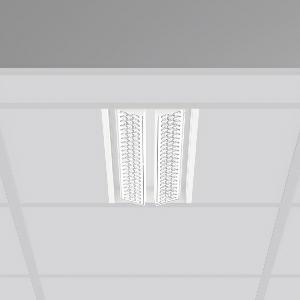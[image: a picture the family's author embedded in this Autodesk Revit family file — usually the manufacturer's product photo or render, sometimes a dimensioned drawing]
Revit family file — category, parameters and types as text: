
# Revit family: tx-move_901736_002_25e7
name_source: partatom
category: Lighting Fixtures
units: mm (PartAtom-declared; Revit-internal decimal feet)

## family parameters
Cut with Voids When Loaded = No
Host = Face
Light Source = No
Part Type = Normal
Room Calculation Point = No
Round Connector Dimension = Use Diameter
Shared = No

## types (1)
- MultiLumen 1 (1 x LED Modul 830, 2750 lm, 3000)
    Apparent Load = 35 VA
    Approval mark = CE
    CIE Flux Codes = 90 97 99 100 100
    Color Rendering = 80
    Color Temperature = 3000
    Default Elevation = 1800 mm
    Description = Series: TX-MOVE
Einlege/Einbau-Flächenstrahler. Housing: sheet steel, powder-coated. 2xSwivel range: 90°. High-efficiency LED units with optimum light control thanks to clear plastic (PC) lens optics. Spezielle Mikrostrukturen reduzieren Gelbsaum. Symmetrical light distribution. Suitable for laying in grid ceiling module 625. Connected converter included in separate gearbox.Suitable for through-wiring.MultiLumen: Luminous flux adjustable in 3 steps. Accessories: Mounting frame for installation in suspended ceilings. Environmentally friendly and resource-saving due to replaceable and recyclable components. 
Colour: traffic white, matt (RAL 9016)
Length: 622 mm
Width: 190 mm
Height: 39 mm
Cut-out length: 602 mm
Cut-out width: 174 mm
Recess height: 100 mm
Lamp: LED
Socket: without socket
Colour temperature: 3000K
Colour rendering index (CRI): 80
System power: 35 W
Rated luminous flux: 5500 lm
Luminous efficiency: 157 lm/W
System power 2: 47 W
Rated luminous flux 2: 7100 lm
Luminous efficiency 2: 151 lm/W
System power 3: 68 W
Rated luminous flux 3: 9700 lm
Luminous efficiency 3: 143 lm/W
Control gear: Regulated power supply
Protection class: I
Type of protection: IP 20
    Height = 0 mm  [stored 0 ft]
    Lamp = 1 x LED Modul 830
    Lamp Light Flux = 2750 lm
    Lamp count = 1
    Length = 622 mm
    Lifetime = 50000 h
    Luminous efficacy = 157 lm/W
    Manufacturer = RZB
    ModVariant = No
    Model = 901736.002
    Mounting Place = Ceiling, Wall
    Mounting Type = Recessed
    Number of Poles = 1
    OnlyDefault = Yes
    Power Factor = 1
    Product Name = TX-MOVE
    Product group = Recessed projectors
    ProductGroupID = 401
    Protection Class = Protection class I
    Protection Degree = IP 20
    RLX_Detail_Level = 1
    RLX_Emergency_Light_Flux = 0 lm
    RLX_Emergency_Type = 0
    RLX_Emergency_Type_DB = No
    RlxData = <blob elided: 34093 chars, md5=c9e92414>
    Socket = socket
    Standby Power = 0 W
    System Light Flux = 5500 lm
    System Power = 35 W
    Type Comments = MultiLumen 1
    Type Image = 901737.002.jpg
    URL = http://relux.com
    VarID = multilumen_1
    Voltage = 230 V
    Voltage Range = 220-240 V
    Weight = 0.00 kg
    Width = 190 mm  [stored 0.62336 ft]

note: [stored X ft] marks values corroborated as IEEE doubles in the binary element streams (Revit-internal decimal feet)

## geometry (parser evidence)
native form markers: Blend x4, Sweep x15
no freeform markers — native parametric forms only
